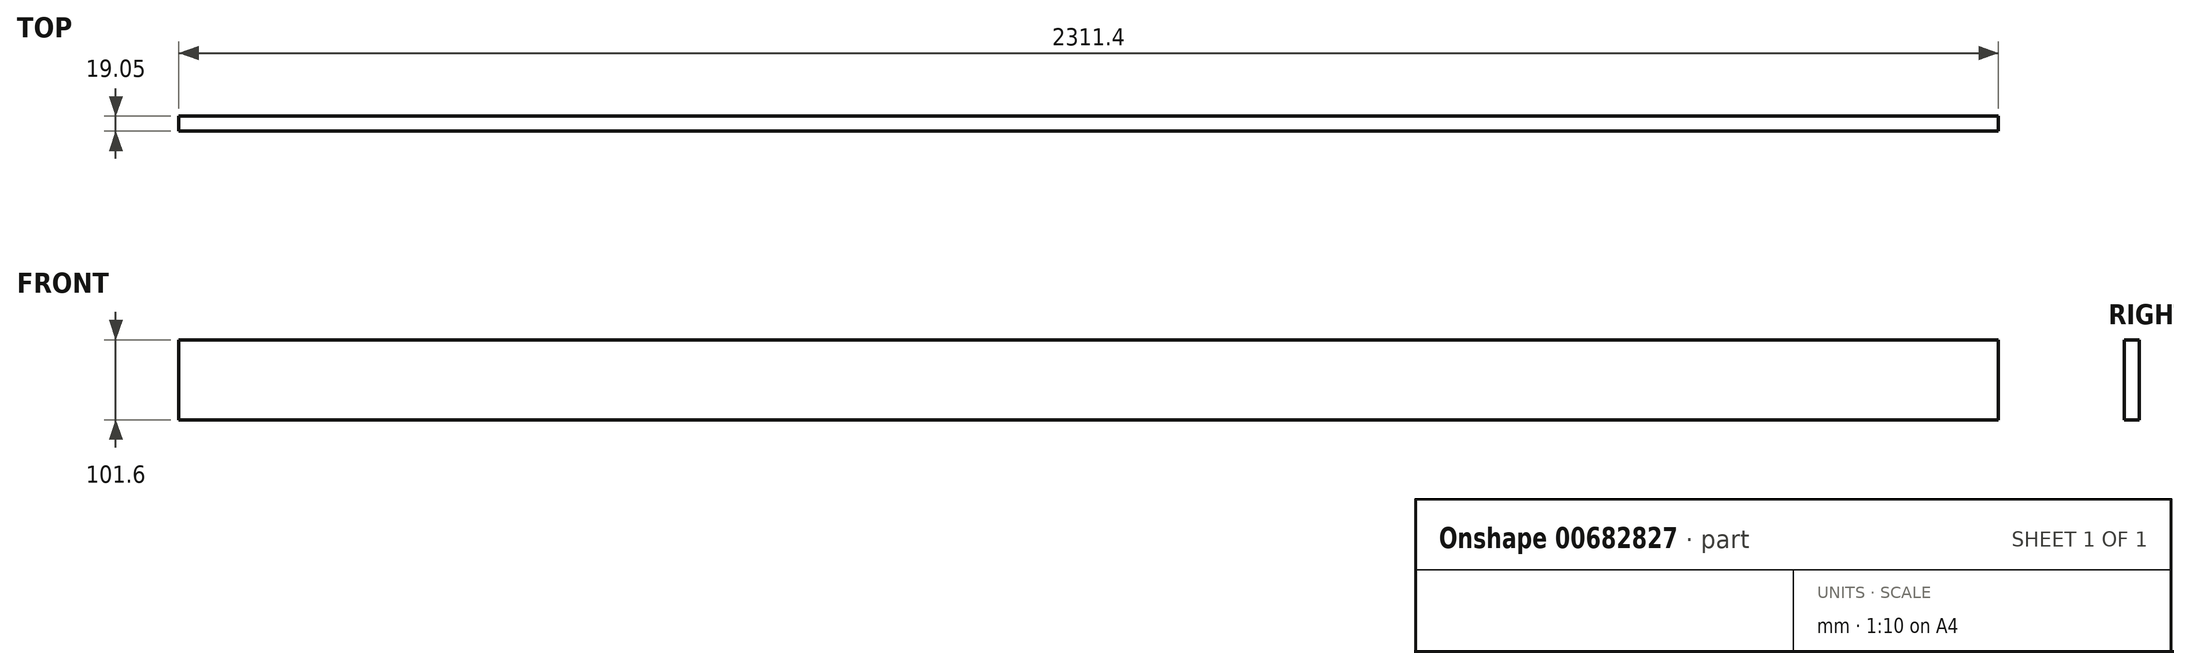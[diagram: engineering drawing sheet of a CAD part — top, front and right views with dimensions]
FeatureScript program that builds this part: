
annotation { "Feature Type Name" : "Feature", "Feature Type Description" : "" }
export const myFeature = defineFeature(function(context is Context, id is Id, definition is map)
    precondition{}
    {
        {
            var Q0;
            Q0=qCreatedBy(makeId("Front.planeOp"),FACE);
            var sketch = newSketch(context, id + "F0", { "sketchPlane" : qUnion([Q0])});
            skLineSegment(sketch, "E0.bottom", {"start": v(0, 0) * mm, "end": v(-2311.4, 0) * mm});
            skLineSegment(sketch, "E0.top", {"start": v(0, 101.6) * mm, "end": v(-2311.4, 101.6) * mm});
            skLineSegment(sketch, "E0.left", {"start": v(0, 0) * mm, "end": v(0, 101.6) * mm});
            skLineSegment(sketch, "E0.right", {"start": v(-2311.4, 0) * mm, "end": v(-2311.4, 101.6) * mm});
            skSolve(sketch);
        }
        {
            var Q0;
            Q0=qSketchRegion(id+"F0",true);
            extrude(context, id + "F1", {"entities" : qUnion([Q0]), "depth" : 19.05 * mm, "offsetDistance" : 25.4 * mm});
        }
    });
